# Revit family: Legrand_Hotel_UX_TOUCH_Detecteur_de_Mouvement
name_source: partatom
category: Equipement électrique
units: mm (PartAtom-declared; Revit-internal decimal feet)

## family parameters
Configuration du panneau = Deux colonnes, circuits au sein
Cote de connecteur circulaire = Utiliser le diamètre
Couper avec des vides une fois chargée = Non
Hôte = Face
Partagée = Non
Point de calcul de pièce = Non
Type d'élément = Tableau de raccordement

## types (1)
- Détecteur de Mouvement
    Adapté pour une transmission sans fil = Non
    Arrêt forcé = Non
    Champ de détection de diamètre au sol = 5 mm  [stored 0.0164042 ft]
    Classe de protection (IP) = IP42
    Commandable à distance = Non
    Commande CVC = Non
    Condition Générale d'Utilisation = https://export.legrand.com
    Couleur = blanc
    Description = Détecteur de Mouvement
    Elévation par défaut = 2500 mm  [stored 8.2021 ft]
    Entrée de poste auxiliaire = Non
    Exécution - Modèle = détecteur de mouvement
    Fabricant = Legrand
    Fonction d'alarme = Non
    Fonction de variation avec insert variateur = Non
    Hauteur de montage optimale = 3 mm  [stored 0.00984252 ft]
    Hauteur hors tout = 38 mm  [stored 0.124672 ft]
    Largeur hors tout = 38 mm  [stored 0.124672 ft]
    Luminosité de déclenchement ajustable = Non
    Matériau = LEGRAND - Plastique blanc
    Modèle = 048778
    Numéro RAL (équivalent) = 9003
    Puissance de coupure  max. = 0,3
    Régulation de la lumière constante = Non
    Sensibilité de réponse ajustable = Non
    Température MIN-MAX (°C) = -5-45
    Tension nominale (V) = 12
    Type de capteur = infrarouge passif
    Type de montage = encastré
    Type de tension = CC
    URL = http://www.legrandoc.com

note: [stored X ft] marks values corroborated as IEEE doubles in the binary element streams (Revit-internal decimal feet)
